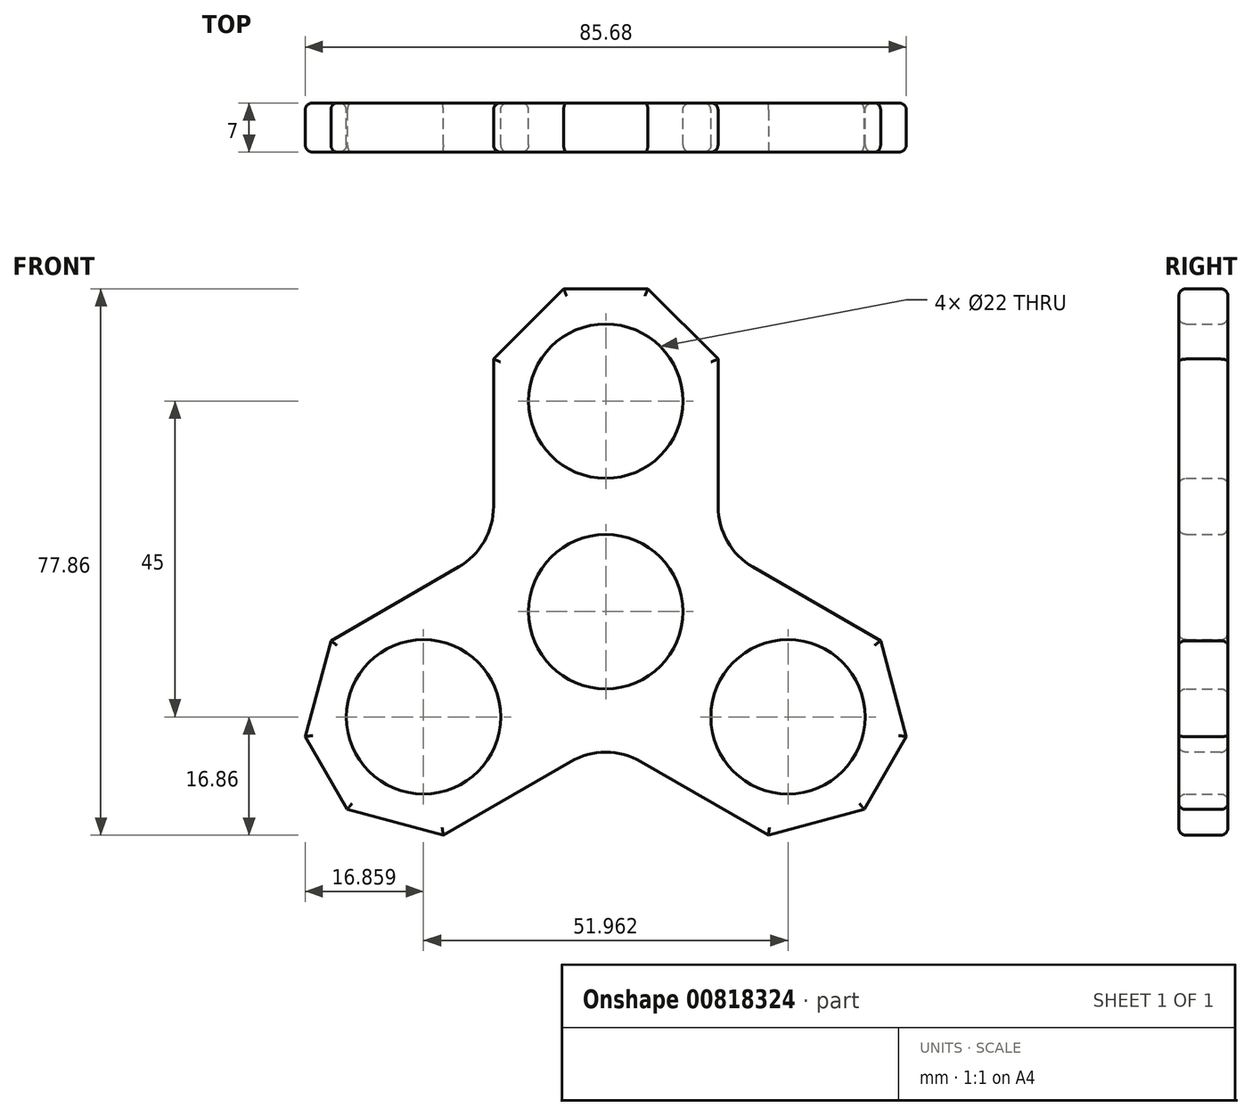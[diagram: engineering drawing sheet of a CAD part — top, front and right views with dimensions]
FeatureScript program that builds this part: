
annotation { "Feature Type Name" : "Feature", "Feature Type Description" : "" }
export const myFeature = defineFeature(function(context is Context, id is Id, definition is map)
    precondition{}
    {
        {
            var Q0;
            Q0=qCreatedBy(makeId("Front.planeOp"),FACE);
            var sketch = newSketch(context, id + "F0", { "sketchPlane" : qUnion([Q0])});
            skCircle(sketch, "E0", {"center": v(0, 0) * mm, "radius": 11 * mm});
            skCircle(sketch, "E1", {"center": v(0, 30) * mm, "radius": 11 * mm});
            skArc(sketch, "E2", {"start": v(-16, 0) * mm, "mid": v(0, -16) * mm, "end": v(16, 0) * mm});
            skLineSegment(sketch, "E3", {"start": v(-16, 0) * mm, "end": v(-16, 46) * mm});
            skLineSegment(sketch, "E4", {"start": v(-16, 46) * mm, "end": v(16, 46) * mm});
            skLineSegment(sketch, "E5", {"start": v(16, 0) * mm, "end": v(16, 46) * mm});
            skSolve(sketch);
        }
        {
            var Q0;
            Q0 = qSketchRegion(id + "F0", true);
            extrude(context, id + "F1", {"entities" : qUnion([Q0]), "depth" : 7 * mm, "offsetDistance" : 25 * mm});
        }
        {
            var Q0;
            Q0=makeQuery(id+"F1.opExtrude","SWEPT_BODY",BODY,{"disambiguationData":[OSD([sQuery(id+"F0.wireOp",EDGE,"E0"),sQuery(id+"F0.wireOp",EDGE,"E1"),sQuery(id+"F0.wireOp",EDGE,"E2"),sQuery(id+"F0.wireOp",EDGE,"E3"),sQuery(id+"F0.wireOp",EDGE,"E4"),sQuery(id+"F0.wireOp",EDGE,"E5")])]});
            var Q1;
            Q1=makeQuery(id+"F1.opExtrude","CAP_EDGE",EDGE,{"disambiguationData":[OSD([sQuery(id+"F0.wireOp",EDGE,"E0")])],"isStart":false});
            circularPattern(context, id + "F2", {"entities" : qUnion([Q0]), "axis" : qUnion([Q1]), "angle" : 360 * degree, "instanceCount" : 3, "equalSpace" : true});
        }
        {
            var Q0;
            Q0=makeQuery(id+"F1.opExtrude","SWEPT_BODY",BODY,{"disambiguationData":[OSD([sQuery(id+"F0.wireOp",EDGE,"E0"),sQuery(id+"F0.wireOp",EDGE,"E1"),sQuery(id+"F0.wireOp",EDGE,"E2"),sQuery(id+"F0.wireOp",EDGE,"E3"),sQuery(id+"F0.wireOp",EDGE,"E4"),sQuery(id+"F0.wireOp",EDGE,"E5")])]});
            var Q1;
            Q1=makeQuery(id+"F2.opPattern","COPY",BODY,{"derivedFrom":makeQuery(id+"F1.opExtrude","SWEPT_BODY",BODY,{"disambiguationData":[OSD([sQuery(id+"F0.wireOp",EDGE,"E0"),sQuery(id+"F0.wireOp",EDGE,"E1"),sQuery(id+"F0.wireOp",EDGE,"E2"),sQuery(id+"F0.wireOp",EDGE,"E3"),sQuery(id+"F0.wireOp",EDGE,"E4"),sQuery(id+"F0.wireOp",EDGE,"E5")])]}),"instanceName":"1"});
            var Q2;
            Q2=makeQuery(id+"F2.opPattern","COPY",BODY,{"derivedFrom":makeQuery(id+"F1.opExtrude","SWEPT_BODY",BODY,{"disambiguationData":[OSD([sQuery(id+"F0.wireOp",EDGE,"E0"),sQuery(id+"F0.wireOp",EDGE,"E1"),sQuery(id+"F0.wireOp",EDGE,"E2"),sQuery(id+"F0.wireOp",EDGE,"E3"),sQuery(id+"F0.wireOp",EDGE,"E4"),sQuery(id+"F0.wireOp",EDGE,"E5")])]}),"instanceName":"2"});
            booleanBodies(context, id + "F3", {"operationType" : BooleanOperationType.UNION, "tools" : qUnion([Q0, Q1, Q2])});
        }
        {
            var Q0;
            Q0=makeQuery(id+"F3.opBoolean","INTERSECT",EDGE,{"derivedFrom":[makeQuery(id+"F1.opExtrude","SWEPT_FACE",FACE,{"disambiguationData":[OSD([sQuery(id+"F0.wireOp",EDGE,"E3")])]}),makeQuery(id+"F2.opPattern","COPY",FACE,{"derivedFrom":makeQuery(id+"F1.opExtrude","SWEPT_FACE",FACE,{"disambiguationData":[OSD([sQuery(id+"F0.wireOp",EDGE,"E5")])]}),"instanceName":"1"})]});
            var Q1;
            Q1=makeQuery(id+"F3.opBoolean","INTERSECT",EDGE,{"derivedFrom":[makeQuery(id+"F2.opPattern","COPY",FACE,{"derivedFrom":makeQuery(id+"F1.opExtrude","SWEPT_FACE",FACE,{"disambiguationData":[OSD([sQuery(id+"F0.wireOp",EDGE,"E3")])]}),"instanceName":"1"}),makeQuery(id+"F2.opPattern","COPY",FACE,{"derivedFrom":makeQuery(id+"F1.opExtrude","SWEPT_FACE",FACE,{"disambiguationData":[OSD([sQuery(id+"F0.wireOp",EDGE,"E5")])]}),"instanceName":"2"})]});
            var Q2;
            Q2=makeQuery(id+"F3.opBoolean","INTERSECT",EDGE,{"derivedFrom":[makeQuery(id+"F1.opExtrude","SWEPT_FACE",FACE,{"disambiguationData":[OSD([sQuery(id+"F0.wireOp",EDGE,"E5")])]}),makeQuery(id+"F2.opPattern","COPY",FACE,{"derivedFrom":makeQuery(id+"F1.opExtrude","SWEPT_FACE",FACE,{"disambiguationData":[OSD([sQuery(id+"F0.wireOp",EDGE,"E3")])]}),"instanceName":"2"})]});
            fillet(context, id + "F4", {"entities" : qUnion([Q0, Q1, Q2]), "radius" : 10 * mm, "tangentPropagation" : true, "allowEdgeOverflow" : false});
        }
        {
            var Q0;
            Q0=makeQuery(id+"F1.opExtrude","SWEPT_EDGE",EDGE,{"disambiguationData":[OSD([sQuery(id+"F0.wireOp",EDGE,"E3"),sQuery(id+"F0.wireOp",EDGE,"E4")])]});
            var Q1;
            Q1=makeQuery(id+"F1.opExtrude","SWEPT_EDGE",EDGE,{"disambiguationData":[OSD([sQuery(id+"F0.wireOp",EDGE,"E4"),sQuery(id+"F0.wireOp",EDGE,"E5")])]});
            var Q2;
            Q2=makeQuery(id+"F2.opPattern","COPY",EDGE,{"derivedFrom":makeQuery(id+"F1.opExtrude","SWEPT_EDGE",EDGE,{"disambiguationData":[OSD([sQuery(id+"F0.wireOp",EDGE,"E3"),sQuery(id+"F0.wireOp",EDGE,"E4")])]}),"instanceName":"2"});
            var Q3;
            Q3=makeQuery(id+"F2.opPattern","COPY",EDGE,{"derivedFrom":makeQuery(id+"F1.opExtrude","SWEPT_EDGE",EDGE,{"disambiguationData":[OSD([sQuery(id+"F0.wireOp",EDGE,"E4"),sQuery(id+"F0.wireOp",EDGE,"E5")])]}),"instanceName":"2"});
            var Q4;
            Q4=makeQuery(id+"F2.opPattern","COPY",EDGE,{"derivedFrom":makeQuery(id+"F1.opExtrude","SWEPT_EDGE",EDGE,{"disambiguationData":[OSD([sQuery(id+"F0.wireOp",EDGE,"E3"),sQuery(id+"F0.wireOp",EDGE,"E4")])]}),"instanceName":"1"});
            var Q5;
            Q5=makeQuery(id+"F2.opPattern","COPY",EDGE,{"derivedFrom":makeQuery(id+"F1.opExtrude","SWEPT_EDGE",EDGE,{"disambiguationData":[OSD([sQuery(id+"F0.wireOp",EDGE,"E4"),sQuery(id+"F0.wireOp",EDGE,"E5")])]}),"instanceName":"1"});
            chamfer(context, id + "F5", {"entities" : qUnion([Q0, Q1, Q2, Q3, Q4, Q5]), "width" : 10 * mm, "tangentPropagation" : true});
        }
        {
            var Q0;
            {var subQ0=makeQuery(id+"F1.opExtrude","CAP_FACE",FACE,{"disambiguationData":[OSD([sQuery(id+"F0.wireOp",EDGE,"E0"),sQuery(id+"F0.wireOp",EDGE,"E1"),sQuery(id+"F0.wireOp",EDGE,"E2"),sQuery(id+"F0.wireOp",EDGE,"E3"),sQuery(id+"F0.wireOp",EDGE,"E4"),sQuery(id+"F0.wireOp",EDGE,"E5")])],"isStart":false});Q0=makeQuery(id+"F3.opBoolean","MERGE",FACE,{"derivedFrom":[subQ0,makeQuery(id+"F2.opPattern","COPY",FACE,{"derivedFrom":subQ0,"instanceName":"1"}),makeQuery(id+"F2.opPattern","COPY",FACE,{"derivedFrom":subQ0,"instanceName":"2"})]});}
            var Q1;
            {var subQ0=makeQuery(id+"F1.opExtrude","CAP_FACE",FACE,{"disambiguationData":[OSD([sQuery(id+"F0.wireOp",EDGE,"E0"),sQuery(id+"F0.wireOp",EDGE,"E1"),sQuery(id+"F0.wireOp",EDGE,"E2"),sQuery(id+"F0.wireOp",EDGE,"E3"),sQuery(id+"F0.wireOp",EDGE,"E4"),sQuery(id+"F0.wireOp",EDGE,"E5")])],"isStart":true});Q1=makeQuery(id+"F3.opBoolean","MERGE",FACE,{"derivedFrom":[subQ0,makeQuery(id+"F2.opPattern","COPY",FACE,{"derivedFrom":subQ0,"instanceName":"1"}),makeQuery(id+"F2.opPattern","COPY",FACE,{"derivedFrom":subQ0,"instanceName":"2"})]});}
            fillet(context, id + "F6", {"entities" : qUnion([Q0, Q1]), "radius" : 1 * mm, "tangentPropagation" : true, "allowEdgeOverflow" : false});
        }
    });
